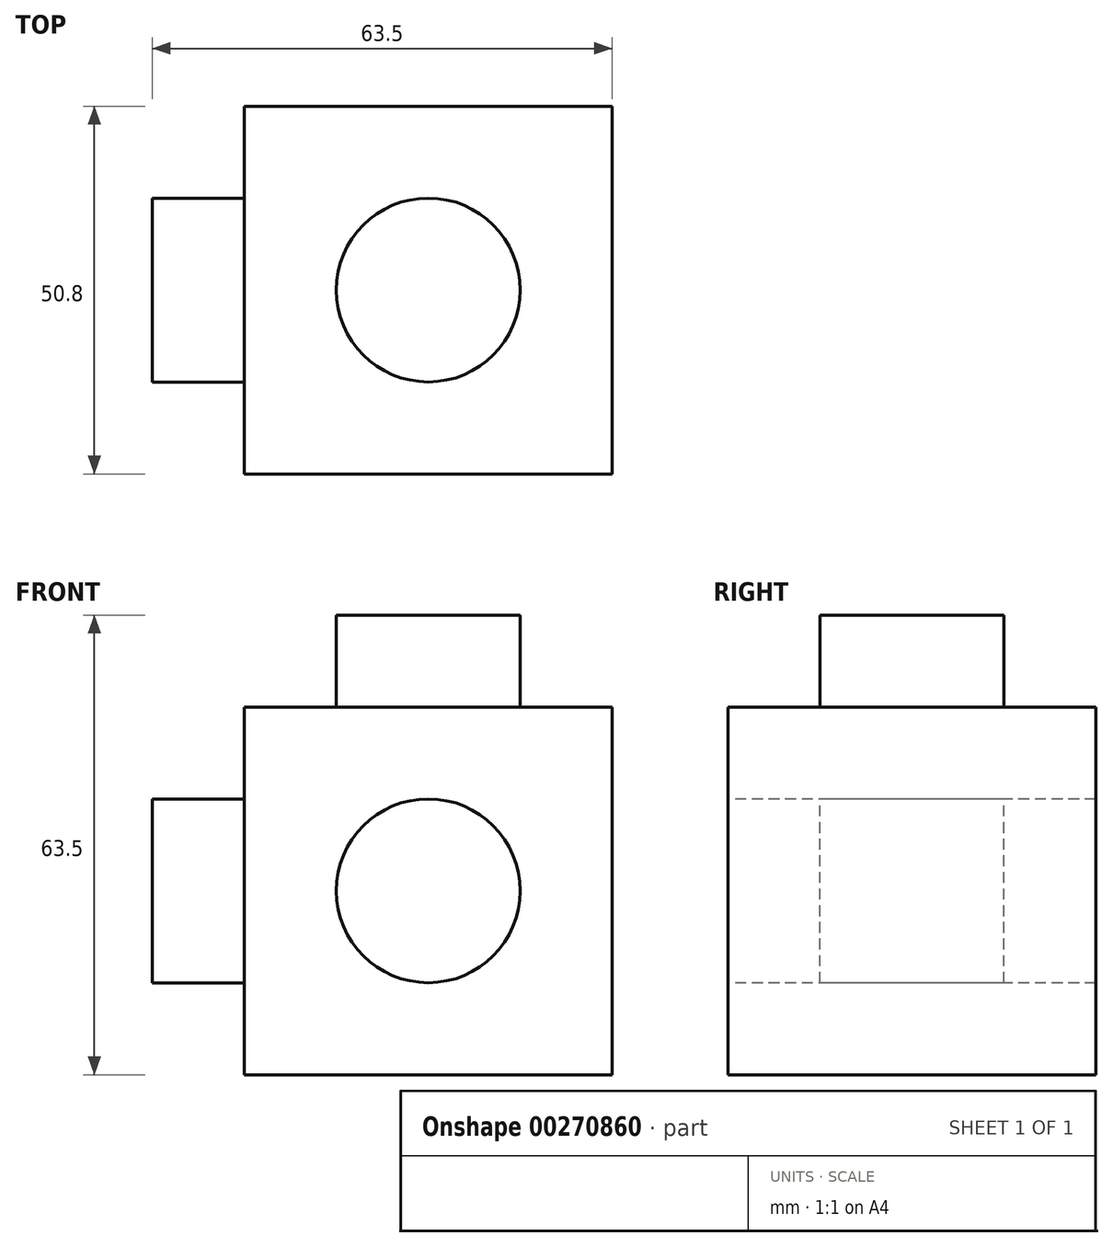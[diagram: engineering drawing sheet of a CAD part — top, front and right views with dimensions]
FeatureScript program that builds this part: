
annotation { "Feature Type Name" : "Feature", "Feature Type Description" : "" }
export const myFeature = defineFeature(function(context is Context, id is Id, definition is map)
    precondition{}
    {
        {
            var Q0;
            Q0=qCreatedBy(makeId("Front.planeOp"),FACE);
            var sketch = newSketch(context, id + "F0", { "sketchPlane" : qUnion([Q0])});
            skLineSegment(sketch, "E0.bottom", {"start": v(-58.25, 65.7) * mm, "end": v(-7.45, 65.7) * mm});
            skLineSegment(sketch, "E0.top", {"start": v(-58.25, 14.9) * mm, "end": v(-7.45, 14.9) * mm});
            skLineSegment(sketch, "E0.left", {"start": v(-58.25, 65.7) * mm, "end": v(-58.25, 14.9) * mm});
            skLineSegment(sketch, "E0.right", {"start": v(-7.45, 65.7) * mm, "end": v(-7.45, 14.9) * mm});
            skSolve(sketch);
        }
        {
            var Q0;
            Q0 = qSketchRegion(id + "F0", true);
            extrude(context, id + "F1", {"entities" : qUnion([Q0]), "depth" : 50.8 * mm});
        }
        {
            var Q0;
            Q0=makeQuery(id+"F1.opExtrude","CAP_FACE",FACE,{"disambiguationData":[OSD([sQuery(id+"F0.wireOp",EDGE,"E0.bottom"),sQuery(id+"F0.wireOp",EDGE,"E0.top"),sQuery(id+"F0.wireOp",EDGE,"E0.left"),sQuery(id+"F0.wireOp",EDGE,"E0.right")])],"isStart":false});
            var sketch = newSketch(context, id + "F2", { "sketchPlane" : qUnion([Q0])});
            skCircle(sketch, "E1", {"center": v(-32.85, 40.3) * mm, "radius": 12.7 * mm});
            skSolve(sketch);
        }
        {
            var Q0;
            Q0=makeQuery(id+"F2.imprint","IMPRINT",FACE,{"disambiguationData":[TD([[makeQuery(id+"F2.imprint","IMPRINT",EDGE,{"derivedFrom":sQuery(id+"F2.wireOp",EDGE,"E1")}),1.0]])]});
            extrude(context, id + "F3", {"entities" : qUnion([Q0]), "operationType" : NewBodyOperationType.REMOVE, "oppositeDirection" : true, "depth" : 50.8 * mm});
        }
        {
            var Q0;
            Q0=makeQuery(id+"F1.opExtrude","SWEPT_FACE",FACE,{"disambiguationData":[OSD([sQuery(id+"F0.wireOp",EDGE,"E0.bottom")])]});
            var sketch = newSketch(context, id + "F4", { "sketchPlane" : qUnion([Q0])});
            skCircle(sketch, "E2", {"center": v(-32.85, -25.4) * mm, "radius": 12.7 * mm});
            skSolve(sketch);
        }
        {
            var Q0;
            Q0=makeQuery(id+"F4.imprint","IMPRINT",FACE,{"disambiguationData":[TD([[makeQuery(id+"F4.imprint","IMPRINT",EDGE,{"derivedFrom":sQuery(id+"F4.wireOp",EDGE,"E2")}),1.0]])]});
            extrude(context, id + "F5", {"entities" : qUnion([Q0]), "operationType" : NewBodyOperationType.ADD, "depth" : 12.7 * mm});
        }
        {
            var Q0;
            Q0=makeQuery(id+"F1.opExtrude","SWEPT_FACE",FACE,{"disambiguationData":[OSD([sQuery(id+"F0.wireOp",EDGE,"E0.left")])]});
            var sketch = newSketch(context, id + "F6", { "sketchPlane" : qUnion([Q0])});
            skLineSegment(sketch, "E3.bottom", {"start": v(12.7, 27.6) * mm, "end": v(38.1, 27.6) * mm});
            skLineSegment(sketch, "E3.top", {"start": v(12.7, 53) * mm, "end": v(38.1, 53) * mm});
            skLineSegment(sketch, "E3.left", {"start": v(12.7, 27.6) * mm, "end": v(12.7, 53) * mm});
            skLineSegment(sketch, "E3.right", {"start": v(38.1, 27.6) * mm, "end": v(38.1, 53) * mm});
            skSolve(sketch);
        }
        {
            var Q0;
            Q0=makeQuery(id+"F6.imprint","IMPRINT",FACE,{"disambiguationData":[TD([[makeQuery(id+"F6.imprint","IMPRINT",EDGE,{"derivedFrom":sQuery(id+"F6.wireOp",EDGE,"E3.bottom")}),1.0]])]});
            extrude(context, id + "F7", {"entities" : qUnion([Q0]), "operationType" : NewBodyOperationType.ADD, "depth" : 12.7 * mm});
        }
    });
